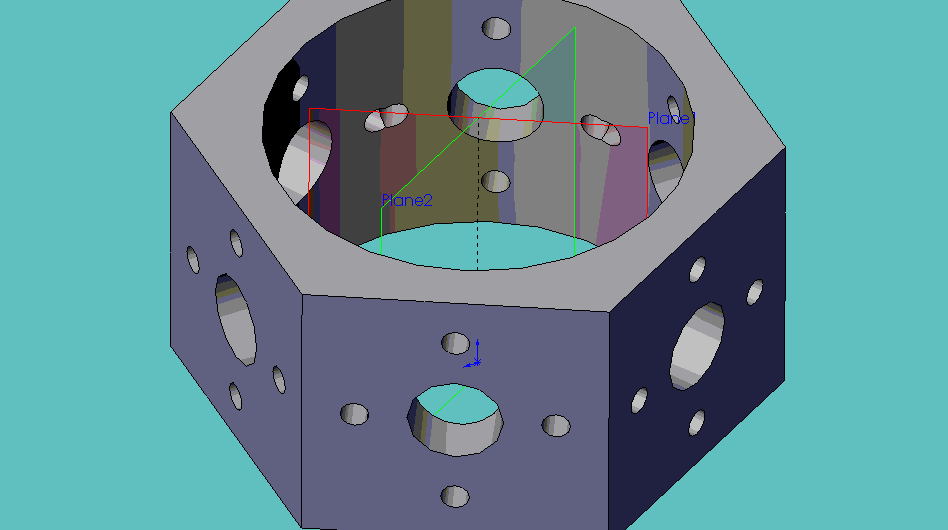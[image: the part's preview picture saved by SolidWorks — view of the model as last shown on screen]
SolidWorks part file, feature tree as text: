
SOLIDWORKS PART (.sldprt)
format: sldprt  version: not decoded by parser v0  size: 235,008 bytes
history: native  units: mm
features: sketch x4, cut_extrude x3, plane x2, material x1, extrude x1 (+12 scaffold rows collapsed)
feature tree (23):
  scaffold x12  (default folders/planes/origin — collapsed)
  material  "Material <not specified>"
  sketch  "Sketch1"  dims[D1=25.4mm]
  extrude  "Extrude1"  Depth=25.4mm
  sketch  "Sketch2"  dims[D1=~1.399711mm]
  cut_extrude  "Cut-Extrude1"  Depth=25.4mm
  plane  "Plane1"
  sketch  "Sketch3"
  cut_extrude  "Cut-Extrude2"  Depth=25.4mm
  plane  "Plane2"
  sketch  "Sketch4"
  cut_extrude  "Cut-Extrude3"  Depth=25.4mm
decode coverage: 6 of 8 modeling features carry decoded parameters
note: ~ marks probable driven/reference dimensions
note: suppression state not decoded; provenance and decode notes live in map.json
